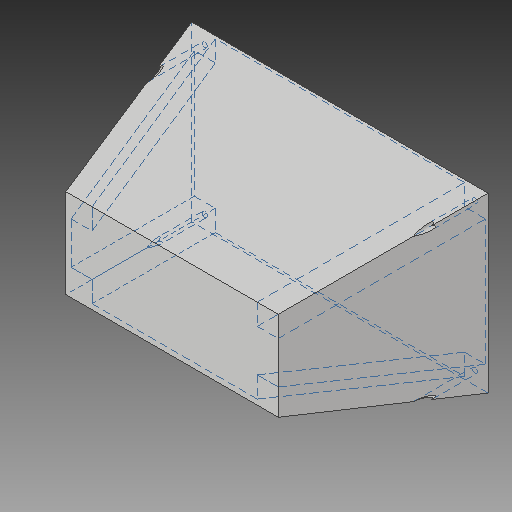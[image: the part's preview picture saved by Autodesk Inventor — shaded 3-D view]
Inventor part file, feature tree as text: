
AUTODESK INVENTOR PART (.ipt)
format: ipt  version: 2019 (Build 230136000, 136)  size: 162,304 bytes
history: native  units: in
note: dims shown in document units (in); Inventor stores cm internally (conversion verified against a paired STEP export)
features: sketch x5, plane x2, loft x2, extrude x1
ambient origin geometry x8: Origin, YZ Plane, XZ Plane, XY Plane, X Axis, Y Axis, Z Axis, Center Point
bodies: Solid1 (feature_tree)
feature tree (10):
  sketch  "Sketch1"  dims[d0=14.125in d1=8.25in]
  plane  "Work Plane1"
  loft  "Loft1"
  sketch  "Sketch3"  dims[d4=2.0in d5=0.0in d6=90.0deg]
  plane  "Work Plane2"
  loft  "Loft2"
  extrude  "Extrusion1"  TaperAngle=0.0deg  [1 undecoded]
  sketch  "Sketch2"  dims[d2=8.0in d3=2.0in]
  sketch  "Sketch5"  dims[d7=0.0in d8=90.0deg]
  sketch  "Sketch6"  dims[d9=0.125in d10=0.125in d11=1.0in d12=7.875in d15=0.125in d16=0.0in d17=90.0deg d18=0.0in d19=90.0deg d20=0.5in d21=0.5in d22=0.25in d23=1.0in d24=0.0in]
note: 1 required parameter value undecoded (feature->parameter linkage not recoverable at this tier; creation-order binding heuristic only, values carry confidence <= 0.55)
